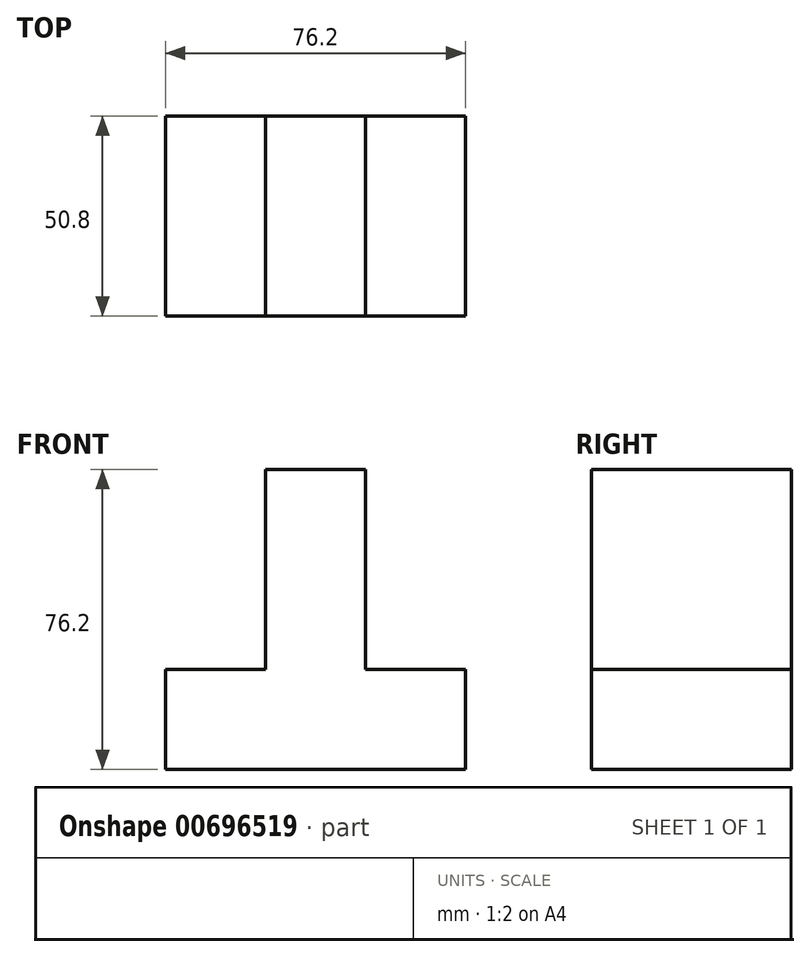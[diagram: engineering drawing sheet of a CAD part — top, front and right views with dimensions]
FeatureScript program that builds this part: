
annotation { "Feature Type Name" : "Feature", "Feature Type Description" : "" }
export const myFeature = defineFeature(function(context is Context, id is Id, definition is map)
    precondition{}
    {
        {
            var Q0;
            Q0=qCreatedBy(makeId("Front.planeOp"),FACE);
            var sketch = newSketch(context, id + "F0", { "sketchPlane" : qUnion([Q0])});
            skLineSegment(sketch, "E0", {"start": v(0, 0) * mm, "end": v(0, -25.4) * mm});
            skLineSegment(sketch, "E1", {"start": v(0, -25.4) * mm, "end": v(76.2, -25.4) * mm});
            skLineSegment(sketch, "E2", {"start": v(76.2, -25.4) * mm, "end": v(76.2, 0) * mm});
            skLineSegment(sketch, "E3", {"start": v(76.2, 0) * mm, "end": v(50.8, 0) * mm});
            skLineSegment(sketch, "E4", {"start": v(50.8, 0) * mm, "end": v(50.8, 50.8) * mm});
            skLineSegment(sketch, "E5", {"start": v(50.8, 50.8) * mm, "end": v(25.4, 50.8) * mm});
            skLineSegment(sketch, "E6", {"start": v(25.4, 50.8) * mm, "end": v(25.4, 0) * mm});
            skLineSegment(sketch, "E7", {"start": v(25.4, 0) * mm, "end": v(0, 0) * mm});
            skSolve(sketch);
        }
        {
            var Q0;
            Q0 = qSketchRegion(id + "F0", true);
            extrude(context, id + "F1", {"entities" : qUnion([Q0]), "depth" : 50.8 * mm, "offsetDistance" : 25.4 * mm});
        }
    });
